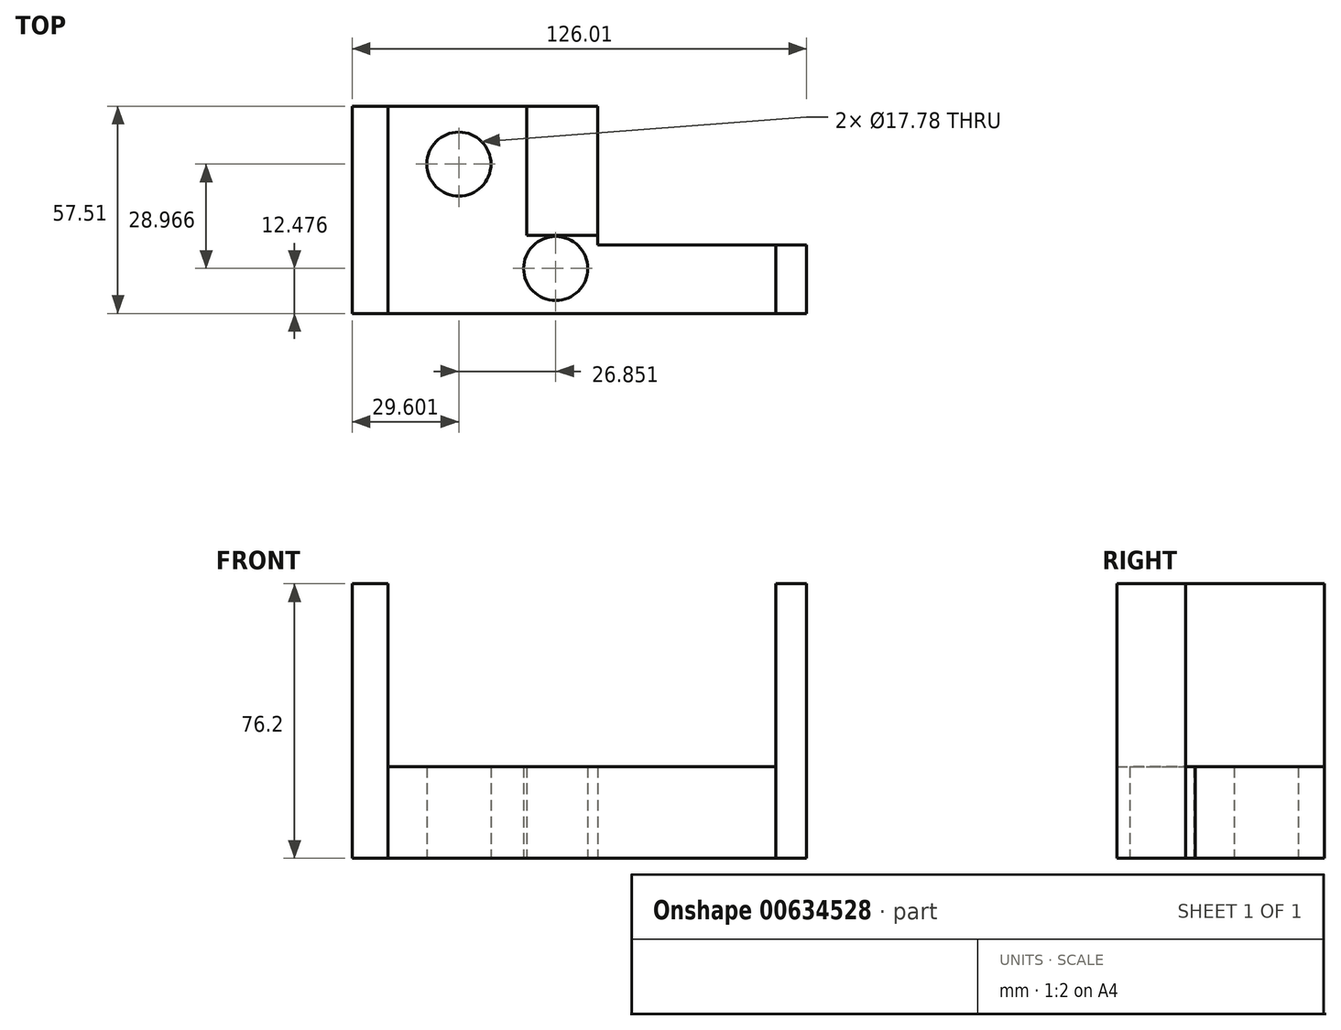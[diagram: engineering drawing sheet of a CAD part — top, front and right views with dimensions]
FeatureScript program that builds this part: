
annotation { "Feature Type Name" : "Feature", "Feature Type Description" : "" }
export const myFeature = defineFeature(function(context is Context, id is Id, definition is map)
    precondition{}
    {
        {
            var Q0;
            Q0=qCreatedBy(makeId("Top.planeOp"),FACE);
            var sketch = newSketch(context, id + "F0", { "sketchPlane" : qUnion([Q0])});
            skLineSegment(sketch, "E0.bottom", {"start": v(-50.68, 18.92) * mm, "end": v(7.46, 18.92) * mm});
            skLineSegment(sketch, "E0.top", {"start": v(-50.68, -38.59) * mm, "end": v(7.46, -38.59) * mm});
            skLineSegment(sketch, "E0.left", {"start": v(-50.68, 18.92) * mm, "end": v(-50.68, -38.59) * mm});
            skLineSegment(sketch, "E0.right", {"start": v(7.46, 18.92) * mm, "end": v(7.46, -38.59) * mm});
            skLineSegment(sketch, "E1.bottom", {"start": v(7.46, -38.59) * mm, "end": v(56.94, -38.59) * mm});
            skLineSegment(sketch, "E1.top", {"start": v(7.46, -19.56) * mm, "end": v(56.94, -19.56) * mm});
            skLineSegment(sketch, "E1.left", {"start": v(7.46, -38.59) * mm, "end": v(7.46, -19.56) * mm});
            skLineSegment(sketch, "E1.right", {"start": v(56.94, -38.59) * mm, "end": v(56.94, -19.56) * mm});
            skLineSegment(sketch, "E2.bottom", {"start": v(56.94, -19.56) * mm, "end": v(65.4, -19.56) * mm});
            skLineSegment(sketch, "E2.top", {"start": v(56.94, -38.59) * mm, "end": v(65.4, -38.59) * mm});
            skLineSegment(sketch, "E2.left", {"start": v(56.94, -19.56) * mm, "end": v(56.94, -38.59) * mm});
            skLineSegment(sketch, "E2.right", {"start": v(65.4, -19.56) * mm, "end": v(65.4, -38.59) * mm});
            skLineSegment(sketch, "E3.bottom", {"start": v(-50.68, -38.59) * mm, "end": v(-60.62, -38.59) * mm});
            skLineSegment(sketch, "E3.top", {"start": v(-50.68, 18.92) * mm, "end": v(-60.62, 18.92) * mm});
            skLineSegment(sketch, "E3.left", {"start": v(-50.68, -38.59) * mm, "end": v(-50.68, 18.92) * mm});
            skLineSegment(sketch, "E3.right", {"start": v(-60.62, -38.59) * mm, "end": v(-60.62, 18.92) * mm});
            skCircle(sketch, "E4", {"center": v(-4.17, -26.11) * mm, "radius": 8.89 * mm});
            skCircle(sketch, "E5", {"center": v(-31.02, 2.85) * mm, "radius": 8.9 * mm});
            skLineSegment(sketch, "E6", {"start": v(-12.22, 18.92) * mm, "end": v(-12.22, -12.13) * mm});
            skLineSegment(sketch, "E7", {"start": v(-12.22, -12.13) * mm, "end": v(-12.22, -16.9) * mm});
            skLineSegment(sketch, "E8", {"start": v(-12.22, -16.9) * mm, "end": v(7.46, -16.9) * mm});
            skSolve(sketch);
        }
        {
            var Q0;
            Q0=makeQuery(id+"F0.imprint","IMPRINT",FACE,{"disambiguationData":[TD([[makeQuery(id+"F0.imprint","IMPRINT",EDGE,{"derivedFrom":sQuery(id+"F0.wireOp",EDGE,"E0.bottom")}),-1.0]])]});
            extrude(context, id + "F1", {"entities" : qUnion([Q0]), "depth" : 25.4 * mm, "offsetDistance" : 25.4 * mm});
        }
        {
            var Q0;
            Q0=makeQuery(id+"F0.imprint","IMPRINT",FACE,{"disambiguationData":[TD([[makeQuery(id+"F0.imprint","IMPRINT",EDGE,{"derivedFrom":sQuery(id+"F0.wireOp",EDGE,"E2.bottom")}),-1.0]])]});
            var Q1;
            Q1=makeQuery(id+"F0.imprint","IMPRINT",FACE,{"disambiguationData":[TD([[makeQuery(id+"F0.imprint","IMPRINT",EDGE,{"derivedFrom":sQuery(id+"F0.wireOp",EDGE,"E3.bottom")}),-1.0]])]});
            extrude(context, id + "F2", {"entities" : qUnion([Q0, Q1]), "operationType" : NewBodyOperationType.ADD, "depth" : 76.2 * mm, "offsetDistance" : 25.4 * mm});
        }
        {
            var Q0;
            Q0=makeQuery(id+"F0.imprint","IMPRINT",FACE,{"disambiguationData":[TD([[makeQuery(id+"F0.imprint","IMPRINT",EDGE,{"derivedFrom":sQuery(id+"F0.wireOp",EDGE,"E1.bottom")}),1.0]])]});
            var Q1;
            Q1=makeQuery(id+"F0.imprint","IMPRINT",FACE,{"disambiguationData":[TD([[makeQuery(id+"F0.imprint","IMPRINT",EDGE,{"derivedFrom":sQuery(id+"F0.wireOp",EDGE,"E0.top")}),1.0]])]});
            extrude(context, id + "F3", {"entities" : qUnion([Q0, Q1]), "depth" : 25.4 * mm, "offsetDistance" : 25.4 * mm});
        }
    });
